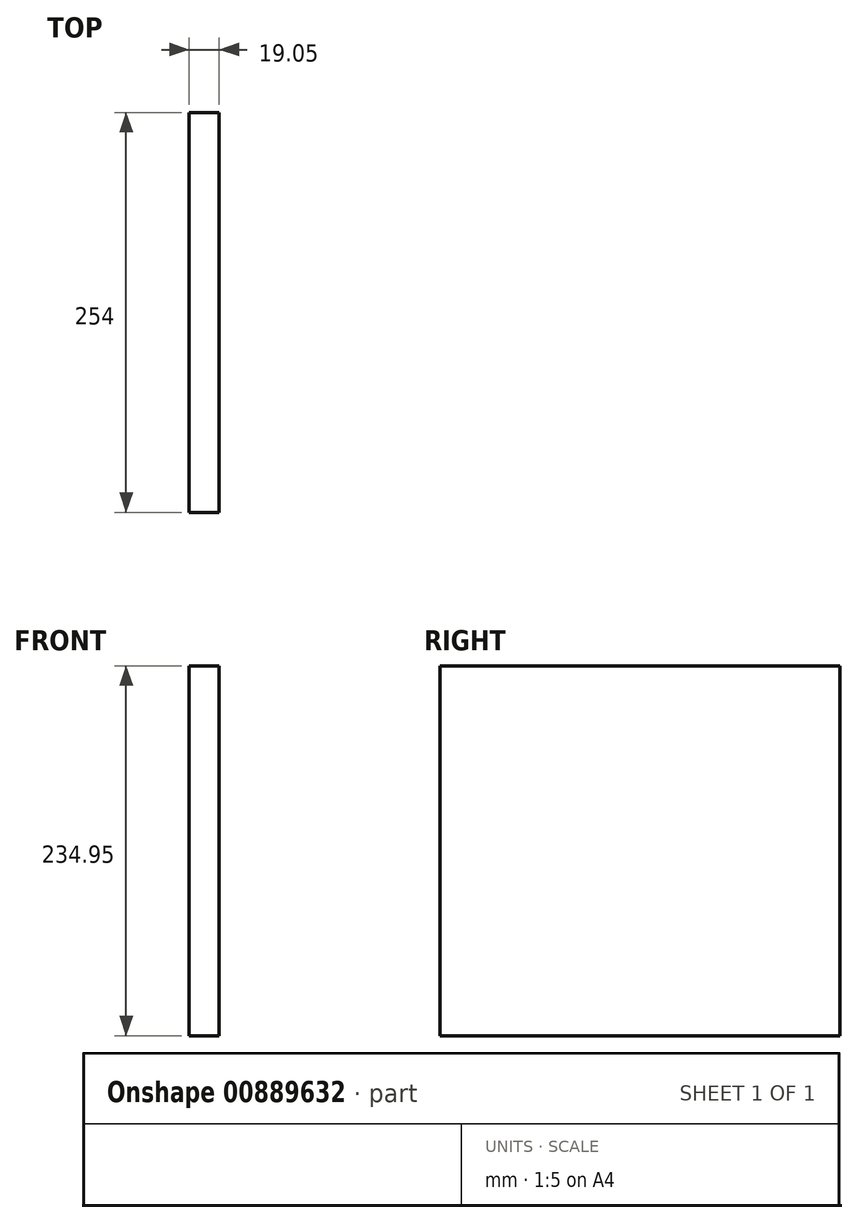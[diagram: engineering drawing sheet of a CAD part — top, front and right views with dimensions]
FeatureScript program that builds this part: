
annotation { "Feature Type Name" : "Feature", "Feature Type Description" : "" }
export const myFeature = defineFeature(function(context is Context, id is Id, definition is map)
    precondition{}
    {
        {
            var Q0;
            Q0=qCreatedBy(makeId("Right.planeOp"),FACE);
            var sketch = newSketch(context, id + "F0", { "sketchPlane" : qUnion([Q0])});
            skLineSegment(sketch, "E0.bottom", {"start": v(0, 0) * mm, "end": v(254, 0) * mm});
            skLineSegment(sketch, "E0.top", {"start": v(0, 234.95) * mm, "end": v(254, 234.95) * mm});
            skLineSegment(sketch, "E0.left", {"start": v(0, 0) * mm, "end": v(0, 234.95) * mm});
            skLineSegment(sketch, "E0.right", {"start": v(254, 0) * mm, "end": v(254, 234.95) * mm});
            skSolve(sketch);
        }
        {
            var Q0;
            Q0 = qSketchRegion(id + "F0", true);
            extrude(context, id + "F1", {"entities" : qUnion([Q0]), "depth" : 19.05 * mm, "offsetDistance" : 25.4 * mm});
        }
    });
